# Revit family: Hekatron_Rauchwarnmelder_Genius Plus X_DE_22.01
name_source: partatom
category: Brandmelder
revit_build: Autodesk Revit 2018 (Build: 20190510_1515(x64)
units: mm (PartAtom-declared; Revit-internal decimal feet)

## family parameters
Basisbauteil = Fläche
Beim Laden mit Abzugskörper schneiden = Nein
Bemaßung runder Anschluss = Durchmesser verwenden
Beschriftungsausrichtung beibehalten = Ja
Gemeinsam genutzt = Nein
OmniClass-Nummer = 23.85.30.21
OmniClass-Titel = Environmental Detection/Registration
Raumberechnungspunkt = Nein
Teiletyp = Normal

## types (1)
- Genius Plus X
    Beschreibung = Rauchwarnmelder incl. Batterie und Zusatzbatterie für optionale Funkvernetzung, für den Einsatz in Wohnhäuser, Wohnungen und Räume mit wohnungsähnlicher Nutzung, sowie in Umgebungen mit erschwerten Bedingungen wie z.B. frostfreien Kellern und Dachstühlen und in Treppenräumen.
    Durchmesser (mm) = 104.0
    Farbe = signalweiß ähnlich RAL 9003
    Funktionsprinzip = optisch, Funk
    Hersteller = Hekatron
    Höhe (mm) = 48.0
    Lautstärke DIN-Ton (dB) = 85.0
    Leistungserklärung (DoP) = CPR-31-19-003-de-en
    Link zu Ausschreibungstext = https://www.meinhplus.de
    Link zu ausschreiben.de = https://www.ausschreiben.de
    Link zum Datenblatt = https://www.hekatron-planungstools.de
    Material = PC-ABS
    Modell = Genius Plus X
    Montageart = Aufputz
    Nettogewicht (g) = 139.0
    Schutzart = IP 40
    Typenkommentare = Rauchwarnmelder Genius Plus X in gestalteter Verpackung
    UB A&S Artikel Nummer = 31-5000030-02-01
    URL = https://www.hekatron-brandschutz.de
    VdS-Anerkennung = G 219068
    Version des BIM Objektes = 22.01
    Vorgabe-Ansicht = 1200 mm
    Zulässige Umgebungstemperatur = 0 °C bis + 55 °C

## geometry (parser evidence)
native form markers: Sweep x2
no freeform markers — native parametric forms only
